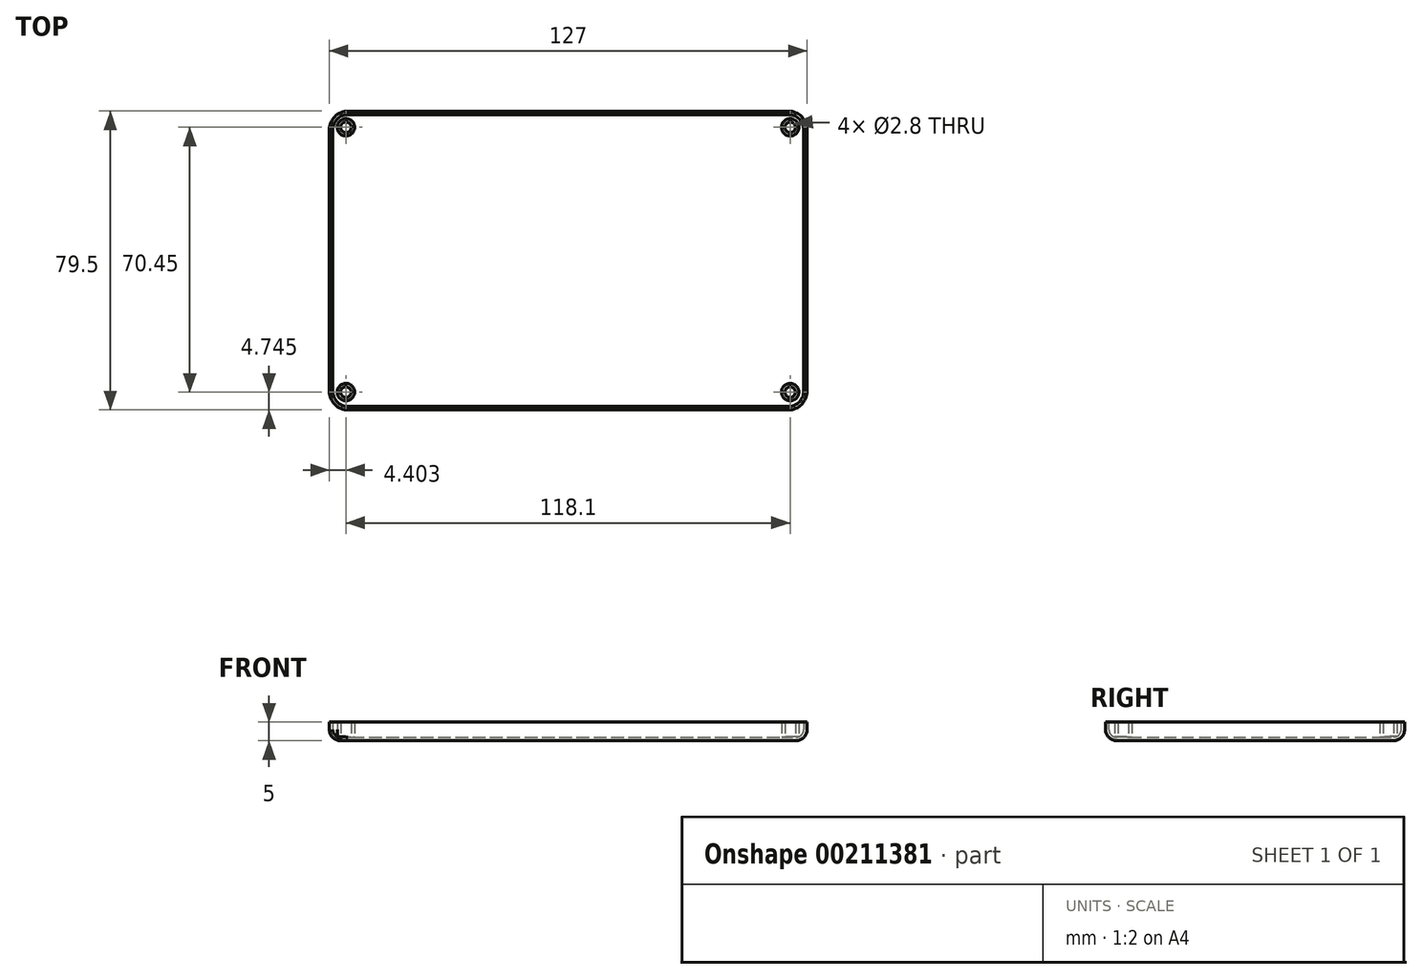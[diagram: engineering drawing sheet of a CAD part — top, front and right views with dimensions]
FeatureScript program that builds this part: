
annotation { "Feature Type Name" : "Feature", "Feature Type Description" : "" }
export const myFeature = defineFeature(function(context is Context, id is Id, definition is map)
    precondition{}
    {
        {
            var Q0;
            Q0=qCreatedBy(makeId("Top.planeOp"),FACE);
            var sketch = newSketch(context, id + "F0", { "sketchPlane" : qUnion([Q0])});
            skLineSegment(sketch, "E0.bottom", {"start": v(-34.2, 53.49) * mm, "end": v(82.8, 53.49) * mm});
            skLineSegment(sketch, "E0.top", {"start": v(-34.2, -26.01) * mm, "end": v(82.8, -26.01) * mm});
            skLineSegment(sketch, "E0.left", {"start": v(-39.2, 48.49) * mm, "end": v(-39.2, -21.01) * mm});
            skLineSegment(sketch, "E0.right", {"start": v(87.8, 48.49) * mm, "end": v(87.8, -21.01) * mm});
            skCircle(sketch, "E1", {"center": v(-34.8, 49.19) * mm, "radius": 1.4 * mm});
            skCircle(sketch, "E2", {"center": v(83.3, 49.19) * mm, "radius": 1.4 * mm});
            skCircle(sketch, "E3", {"center": v(83.3, -21.26) * mm, "radius": 1.4 * mm});
            skCircle(sketch, "E4", {"center": v(-34.8, -21.26) * mm, "radius": 1.4 * mm});
            skPoint(sketch, "E5.visualSharp", {"position": v(87.8, 53.49) * mm});
            skArc(sketch, "E5.filletArc", {"start": v(87.8, 48.49) * mm, "mid": v(86.34, 52.02) * mm, "end": v(82.8, 53.49) * mm});
            skPoint(sketch, "E6.visualSharp", {"position": v(87.8, -26.01) * mm});
            skArc(sketch, "E6.filletArc", {"start": v(82.8, -26.01) * mm, "mid": v(86.34, -24.55) * mm, "end": v(87.8, -21.01) * mm});
            skPoint(sketch, "E7.visualSharp", {"position": v(-39.2, -26.01) * mm});
            skArc(sketch, "E7.filletArc", {"start": v(-39.2, -21.01) * mm, "mid": v(-37.73, -24.55) * mm, "end": v(-34.2, -26.01) * mm});
            skPoint(sketch, "E8.visualSharp", {"position": v(-39.2, 53.49) * mm});
            skArc(sketch, "E8.filletArc", {"start": v(-34.2, 53.49) * mm, "mid": v(-37.73, 52.02) * mm, "end": v(-39.2, 48.49) * mm});
            skSolve(sketch);
        }
        {
            var Q0;
            Q0=makeQuery(id+"F0.imprint","IMPRINT",FACE,{"disambiguationData":[TD([[makeQuery(id+"F0.imprint","IMPRINT",EDGE,{"derivedFrom":sQuery(id+"F0.wireOp",EDGE,"E0.bottom")}),-1.0]])]});
            extrude(context, id + "F1", {"entities" : qUnion([Q0]), "depth" : 5 * mm});
        }
        {
            var Q0;
            Q0=makeQuery(id+"F1.opExtrude","CAP_EDGE",EDGE,{"disambiguationData":[OSD([sQuery(id+"F0.wireOp",EDGE,"E7.filletArc")])],"isStart":true});
            fillet(context, id + "F2", {"entities" : qUnion([Q0]), "radius" : 3 * mm, "tangentPropagation" : true, "allowEdgeOverflow" : false});
        }
        {
            var Q0;
            Q0=makeQuery(id+"F1.opExtrude","CAP_FACE",FACE,{"disambiguationData":[OSD([sQuery(id+"F0.wireOp",EDGE,"E0.bottom"),sQuery(id+"F0.wireOp",EDGE,"E0.top"),sQuery(id+"F0.wireOp",EDGE,"E0.left"),sQuery(id+"F0.wireOp",EDGE,"E0.right"),sQuery(id+"F0.wireOp",EDGE,"E1"),sQuery(id+"F0.wireOp",EDGE,"E2"),sQuery(id+"F0.wireOp",EDGE,"E3"),sQuery(id+"F0.wireOp",EDGE,"E4"),sQuery(id+"F0.wireOp",EDGE,"E5.filletArc"),sQuery(id+"F0.wireOp",EDGE,"E6.filletArc"),sQuery(id+"F0.wireOp",EDGE,"E7.filletArc"),sQuery(id+"F0.wireOp",EDGE,"E8.filletArc")])],"isStart":false});
            var Q1;
            Q1=makeQuery(id+"F1.opExtrude","SWEPT_BODY",BODY,{"disambiguationData":[OSD([sQuery(id+"F0.wireOp",EDGE,"E0.bottom"),sQuery(id+"F0.wireOp",EDGE,"E0.top"),sQuery(id+"F0.wireOp",EDGE,"E0.left"),sQuery(id+"F0.wireOp",EDGE,"E0.right"),sQuery(id+"F0.wireOp",EDGE,"E1"),sQuery(id+"F0.wireOp",EDGE,"E2"),sQuery(id+"F0.wireOp",EDGE,"E3"),sQuery(id+"F0.wireOp",EDGE,"E4"),sQuery(id+"F0.wireOp",EDGE,"E5.filletArc"),sQuery(id+"F0.wireOp",EDGE,"E6.filletArc"),sQuery(id+"F0.wireOp",EDGE,"E7.filletArc"),sQuery(id+"F0.wireOp",EDGE,"E8.filletArc")])]});
            shell(context, id + "F3", {"entities" : qUnion([Q0]), "parts" : qUnion([Q1]), "thickness" : .9 * mm});
        }
    });
